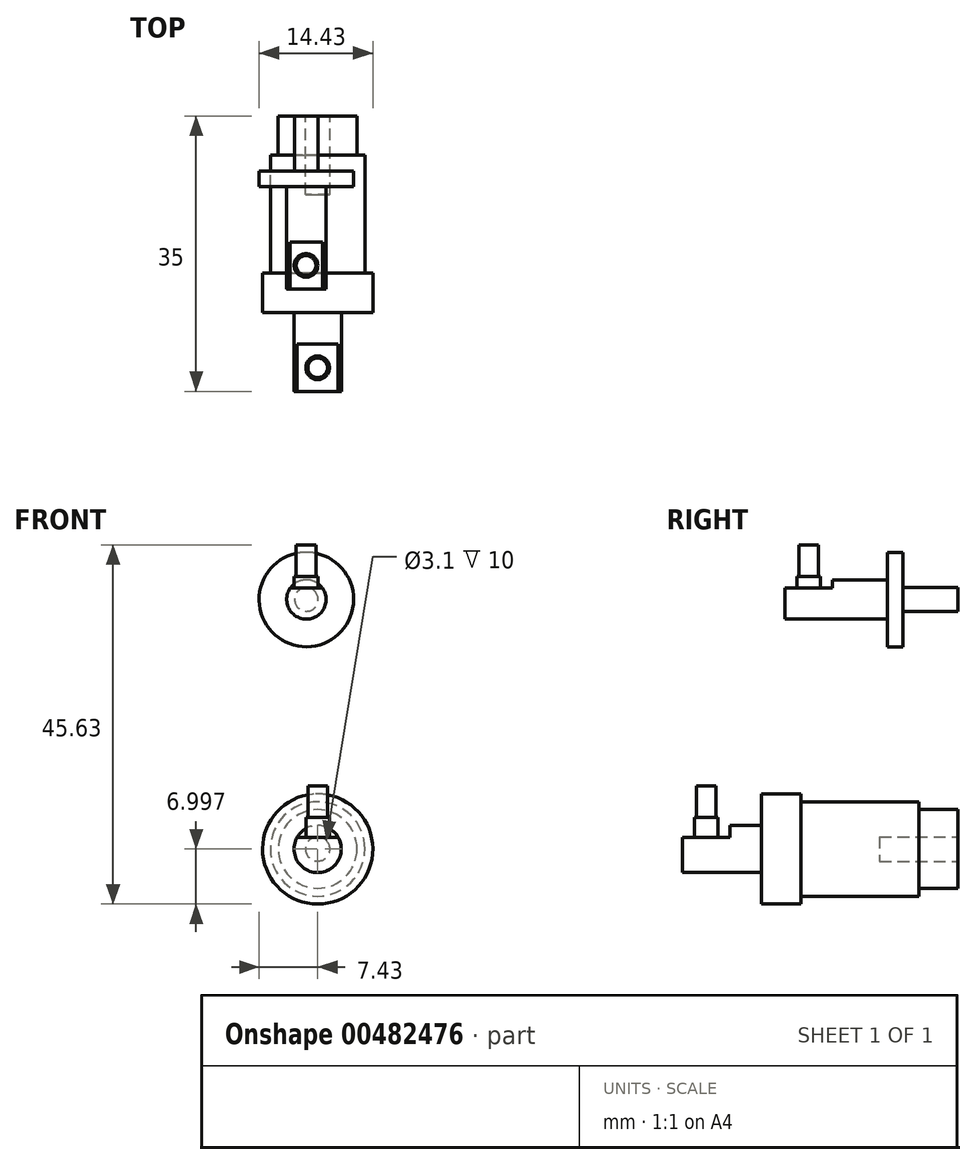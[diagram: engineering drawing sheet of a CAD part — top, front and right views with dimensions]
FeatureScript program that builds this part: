
annotation { "Feature Type Name" : "Feature", "Feature Type Description" : "" }
export const myFeature = defineFeature(function(context is Context, id is Id, definition is map)
    precondition{}
    {
        {
            var Q0;
            Q0=qCreatedBy(makeId("Front.planeOp"),FACE);
            var sketch = newSketch(context, id + "F0", { "sketchPlane" : qUnion([Q0])});
            skCircle(sketch, "E0", {"center": v(-5.52, 39.23) * mm, "radius": 1.5 * mm});
            skSolve(sketch);
        }
        {
            var Q0;
            Q0 = qSketchRegion(id + "F0", true);
            extrude(context, id + "F1", {"entities" : qUnion([Q0]), "depth" : 7 * mm, "offsetDistance" : 25 * mm});
        }
        {
            var Q0;
            Q0=makeQuery(id+"F1.opExtrude","CAP_FACE",FACE,{"disambiguationData":[OSD([sQuery(id+"F0.wireOp",EDGE,"E0")])],"isStart":false});
            var sketch = newSketch(context, id + "F2", { "sketchPlane" : qUnion([Q0])});
            skCircle(sketch, "E1", {"center": v(-5.52, 39.23) * mm, "radius": 2.5 * mm});
            skSolve(sketch);
        }
        {
            var Q0;
            Q0=makeQuery(id+"F2.imprint","IMPRINT",FACE,{"disambiguationData":[TD([[makeQuery(id+"F2.imprint","IMPRINT",EDGE,{"derivedFrom":sQuery(id+"F2.wireOp",EDGE,"E1")}),1.0]])]});
            var Q1;
            Q1=makeQuery(id+"F2.imprint","IMPRINT",FACE,{"disambiguationData":[TD([[makeQuery(id+"F2.imprint","IMPRINT",EDGE,{"derivedFrom":makeQuery(id+"F1.opExtrude","CAP_EDGE",EDGE,{"disambiguationData":[OSD([sQuery(id+"F0.wireOp",EDGE,"E0")])],"isStart":false})}),1.0]])]});
            extrude(context, id + "F3", {"entities" : qUnion([Q0, Q1]), "operationType" : NewBodyOperationType.ADD, "depth" : 15 * mm, "offsetDistance" : 25 * mm});
        }
        {
            var Q0;
            Q0=makeQuery(id+"F3.opExtrude","CAP_FACE",FACE,{"disambiguationData":[OSD([sQuery(id+"F2.wireOp",EDGE,"E1")])],"isStart":false});
            var sketch = newSketch(context, id + "F4", { "sketchPlane" : qUnion([Q0])});
            skLineSegment(sketch, "E2", {"start": v(-7.57, 40.67) * mm, "end": v(-3.48, 40.67) * mm});
            skSolve(sketch);
        }
        {
            var Q0;
            {var subQ0=sQuery(id+"F4.wireOp",EDGE,"E2");Q0=makeQuery(id+"F4.imprint","IMPRINT",FACE,{"disambiguationData":[TD([[makeQuery(id+"F4.imprint","IMPRINT",EDGE,{"derivedFrom":subQ0}),1.0]])]});}
            extrude(context, id + "F5", {"entities" : qUnion([Q0]), "operationType" : NewBodyOperationType.REMOVE, "oppositeDirection" : true, "depth" : 6 * mm, "offsetDistance" : 25 * mm});
        }
        {
            var Q0;
            Q0=makeQuery(id+"F5.boolean.opBoolean","COPY",FACE,{"derivedFrom":makeQuery(id+"F5.opExtrude","SWEPT_FACE",FACE,{"disambiguationData":[OSD([sQuery(id+"F4.wireOp",EDGE,"E2")])]})});
            var sketch = newSketch(context, id + "F6", { "sketchPlane" : qUnion([Q0])});
            skLineSegment(sketch, "E3", {"start": v(-5.57, -22) * mm, "end": v(-5.57, -16) * mm, "construction": true});
            skLineSegment(sketch, "E4", {"start": v(-7.57, -19) * mm, "end": v(-3.48, -19) * mm, "construction": true});
            skCircle(sketch, "E5", {"center": v(-5.57, -19) * mm, "radius": 1.5 * mm});
            skSolve(sketch);
        }
        {
            var Q0;
            Q0 = qSketchRegion(id + "F6", true);
            extrude(context, id + "F7", {"entities" : qUnion([Q0]), "operationType" : NewBodyOperationType.ADD, "depth" : 1.5 * mm, "offsetDistance" : 25 * mm});
        }
        {
            var Q0;
            Q0=makeQuery(id+"F7.opExtrude","CAP_FACE",FACE,{"disambiguationData":[OSD([sQuery(id+"F6.wireOp",EDGE,"E5")])],"isStart":false});
            var sketch = newSketch(context, id + "F8", { "sketchPlane" : qUnion([Q0])});
            skCircle(sketch, "E6", {"center": v(-5.57, -19) * mm, "radius": 1.25 * mm});
            skSolve(sketch);
        }
        {
            var Q0;
            Q0 = qSketchRegion(id + "F8", true);
            extrude(context, id + "F9", {"entities" : qUnion([Q0]), "operationType" : NewBodyOperationType.ADD, "depth" : 4 * mm, "offsetDistance" : 25 * mm});
        }
        {
            var Q0;
            Q0=qCreatedBy(makeId("Front.planeOp"),FACE);
            var sketch = newSketch(context, id + "F10", { "sketchPlane" : qUnion([Q0])});
            skCircle(sketch, "E7", {"center": v(-4.1, 7.54) * mm, "radius": 5 * mm});
            skSolve(sketch);
        }
        {
            var Q0;
            Q0 = qSketchRegion(id + "F10", true);
            extrude(context, id + "F11", {"entities" : qUnion([Q0]), "depth" : 5 * mm, "offsetDistance" : 25 * mm});
        }
        {
            var Q0;
            Q0=makeQuery(id+"F11.opExtrude","CAP_FACE",FACE,{"disambiguationData":[OSD([sQuery(id+"F10.wireOp",EDGE,"E7")])],"isStart":false});
            var sketch = newSketch(context, id + "F12", { "sketchPlane" : qUnion([Q0])});
            skCircle(sketch, "E8", {"center": v(-4.1, 7.54) * mm, "radius": 6 * mm});
            skSolve(sketch);
        }
        {
            var Q0;
            Q0=makeQuery(id+"F12.imprint","IMPRINT",FACE,{"disambiguationData":[TD([[makeQuery(id+"F12.imprint","IMPRINT",EDGE,{"derivedFrom":sQuery(id+"F12.wireOp",EDGE,"E8")}),1.0]])]});
            var Q1;
            Q1=makeQuery(id+"F12.imprint","IMPRINT",FACE,{"disambiguationData":[TD([[makeQuery(id+"F12.imprint","IMPRINT",EDGE,{"derivedFrom":makeQuery(id+"F11.opExtrude","CAP_EDGE",EDGE,{"disambiguationData":[OSD([sQuery(id+"F10.wireOp",EDGE,"E7")])],"isStart":false})}),1.0]])]});
            extrude(context, id + "F13", {"entities" : qUnion([Q0, Q1]), "operationType" : NewBodyOperationType.ADD, "depth" : 15 * mm, "offsetDistance" : 25 * mm});
        }
        {
            var Q0;
            Q0=makeQuery(id+"F13.opExtrude","CAP_FACE",FACE,{"disambiguationData":[OSD([sQuery(id+"F12.wireOp",EDGE,"E8")])],"isStart":false});
            var sketch = newSketch(context, id + "F14", { "sketchPlane" : qUnion([Q0])});
            skCircle(sketch, "E9", {"center": v(-4.1, 7.54) * mm, "radius": 7 * mm});
            skSolve(sketch);
        }
        {
            var Q0;
            Q0=makeQuery(id+"F14.imprint","IMPRINT",FACE,{"disambiguationData":[TD([[makeQuery(id+"F14.imprint","IMPRINT",EDGE,{"derivedFrom":sQuery(id+"F14.wireOp",EDGE,"E9")}),1.0]])]});
            var Q1;
            Q1=makeQuery(id+"F14.imprint","IMPRINT",FACE,{"disambiguationData":[TD([[makeQuery(id+"F14.imprint","IMPRINT",EDGE,{"derivedFrom":makeQuery(id+"F13.opExtrude","CAP_EDGE",EDGE,{"disambiguationData":[OSD([sQuery(id+"F12.wireOp",EDGE,"E8")])],"isStart":false})}),1.0]])]});
            extrude(context, id + "F15", {"entities" : qUnion([Q0, Q1]), "operationType" : NewBodyOperationType.ADD, "depth" : 5 * mm, "offsetDistance" : 25 * mm});
        }
        {
            var Q0;
            Q0=makeQuery(id+"F15.opExtrude","CAP_FACE",FACE,{"disambiguationData":[OSD([sQuery(id+"F14.wireOp",EDGE,"E9")])],"isStart":false});
            var sketch = newSketch(context, id + "F16", { "sketchPlane" : qUnion([Q0])});
            skCircle(sketch, "E10", {"center": v(-4.1, 7.54) * mm, "radius": 3 * mm});
            skSolve(sketch);
        }
        {
            var Q0;
            Q0=makeQuery(id+"F16.imprint","IMPRINT",FACE,{"disambiguationData":[TD([[makeQuery(id+"F16.imprint","IMPRINT",EDGE,{"derivedFrom":sQuery(id+"F16.wireOp",EDGE,"E10")}),1.0]])]});
            extrude(context, id + "F17", {"entities" : qUnion([Q0]), "operationType" : NewBodyOperationType.ADD, "depth" : 10 * mm, "offsetDistance" : 25 * mm});
        }
        {
            var Q0;
            Q0=makeQuery(id+"F17.opExtrude","CAP_FACE",FACE,{"disambiguationData":[OSD([sQuery(id+"F16.wireOp",EDGE,"E10")])],"isStart":false});
            var sketch = newSketch(context, id + "F18", { "sketchPlane" : qUnion([Q0])});
            skLineSegment(sketch, "E11", {"start": v(-6.69, 9.04) * mm, "end": v(-1.5, 9.04) * mm});
            skSolve(sketch);
        }
        {
            var Q0;
            {var subQ0=sQuery(id+"F18.wireOp",EDGE,"E11");Q0=makeQuery(id+"F18.imprint","IMPRINT",FACE,{"disambiguationData":[TD([[makeQuery(id+"F18.imprint","IMPRINT",EDGE,{"derivedFrom":subQ0}),1.0]])]});}
            extrude(context, id + "F19", {"entities" : qUnion([Q0]), "operationType" : NewBodyOperationType.REMOVE, "oppositeDirection" : true, "depth" : 6 * mm, "offsetDistance" : 25 * mm});
        }
        {
            var Q0;
            Q0=makeQuery(id+"F19.boolean.opBoolean","COPY",FACE,{"derivedFrom":makeQuery(id+"F19.opExtrude","SWEPT_FACE",FACE,{"disambiguationData":[OSD([sQuery(id+"F18.wireOp",EDGE,"E11")])]})});
            var sketch = newSketch(context, id + "F20", { "sketchPlane" : qUnion([Q0])});
            skLineSegment(sketch, "E12", {"start": v(-6.69, -32) * mm, "end": v(-1.5, -32) * mm, "construction": true});
            skLineSegment(sketch, "E13", {"start": v(-4.1, -35) * mm, "end": v(-4.1, -29) * mm, "construction": true});
            skCircle(sketch, "E14", {"center": v(-4.1, -32) * mm, "radius": 1.5 * mm});
            skSolve(sketch);
        }
        {
            var Q0;
            Q0=makeQuery(id+"F20.imprint","IMPRINT",FACE,{"disambiguationData":[TD([[makeQuery(id+"F20.imprint","IMPRINT",EDGE,{"derivedFrom":sQuery(id+"F20.wireOp",EDGE,"E14")}),1.0]])]});
            extrude(context, id + "F21", {"entities" : qUnion([Q0]), "operationType" : NewBodyOperationType.ADD, "depth" : 2.5 * mm, "offsetDistance" : 25 * mm});
        }
        {
            var Q0;
            Q0=makeQuery(id+"F21.opExtrude","CAP_FACE",FACE,{"disambiguationData":[OSD([sQuery(id+"F20.wireOp",EDGE,"E14")])],"isStart":false});
            var sketch = newSketch(context, id + "F22", { "sketchPlane" : qUnion([Q0])});
            skCircle(sketch, "E15", {"center": v(-4.1, -32) * mm, "radius": 1.25 * mm});
            skSolve(sketch);
        }
        {
            var Q0;
            Q0 = qSketchRegion(id + "F22", true);
            extrude(context, id + "F23", {"entities" : qUnion([Q0]), "operationType" : NewBodyOperationType.ADD, "depth" : 4 * mm, "offsetDistance" : 25 * mm});
        }
        {
            var Q0;
            Q0=makeQuery(id+"F11.opExtrude","CAP_FACE",FACE,{"disambiguationData":[OSD([sQuery(id+"F10.wireOp",EDGE,"E7")])],"isStart":true});
            var sketch = newSketch(context, id + "F24", { "sketchPlane" : qUnion([Q0])});
            skCircle(sketch, "E16", {"center": v(4.1, 7.54) * mm, "radius": 1.55 * mm});
            skSolve(sketch);
        }
        {
            var Q0;
            Q0=makeQuery(id+"F24.imprint","IMPRINT",FACE,{"disambiguationData":[TD([[makeQuery(id+"F24.imprint","IMPRINT",EDGE,{"derivedFrom":sQuery(id+"F24.wireOp",EDGE,"E16")}),1.0]])]});
            extrude(context, id + "F25", {"entities" : qUnion([Q0]), "operationType" : NewBodyOperationType.REMOVE, "oppositeDirection" : true, "depth" : 10 * mm, "offsetDistance" : 25 * mm});
        }
        {
            var Q0;
            Q0=makeQuery(id+"F3.opExtrude","CAP_FACE",FACE,{"disambiguationData":[OSD([sQuery(id+"F2.wireOp",EDGE,"E1")])],"isStart":true});
            var sketch = newSketch(context, id + "F26", { "sketchPlane" : qUnion([Q0])});
            skCircle(sketch, "E17", {"center": v(5.52, 39.23) * mm, "radius": 6 * mm});
            skSolve(sketch);
        }
        {
            var Q0;
            Q0 = qSketchRegion(id + "F26", true);
            extrude(context, id + "F27", {"entities" : qUnion([Q0]), "operationType" : NewBodyOperationType.ADD, "oppositeDirection" : true, "depth" : 2 * mm, "offsetDistance" : 25 * mm});
        }
    });
